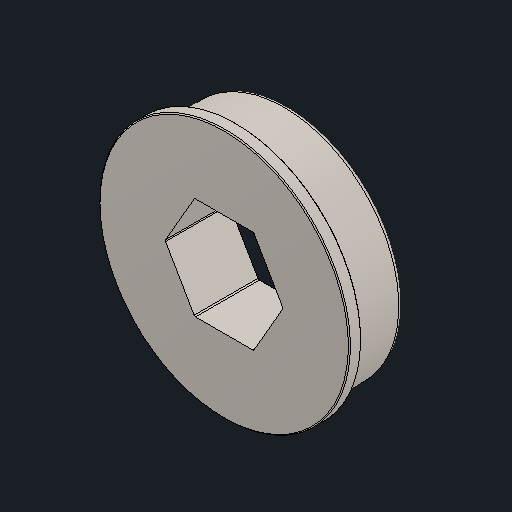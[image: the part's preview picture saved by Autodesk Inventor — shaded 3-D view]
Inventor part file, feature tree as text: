
AUTODESK INVENTOR PART (.ipt)
format: ipt  version: 2023.4 (Build 274418000, 418)  size: 226,816 bytes
history: native  units: in
note: dims shown in document units (in); Inventor stores cm internally (conversion verified against a paired STEP export)
features: fillet x1
ambient origin geometry x8: Origin, YZ Plane, XZ Plane, XY Plane, X Axis, Y Axis, Z Axis, Center Point
bodies: Solid1 (feature_tree)
feature tree (1):
  fillet  "Fillet2"  [1 undecoded]
note: 1 required parameter value undecoded (feature->parameter linkage not recoverable at this tier; creation-order binding heuristic only, values carry confidence <= 0.55)
